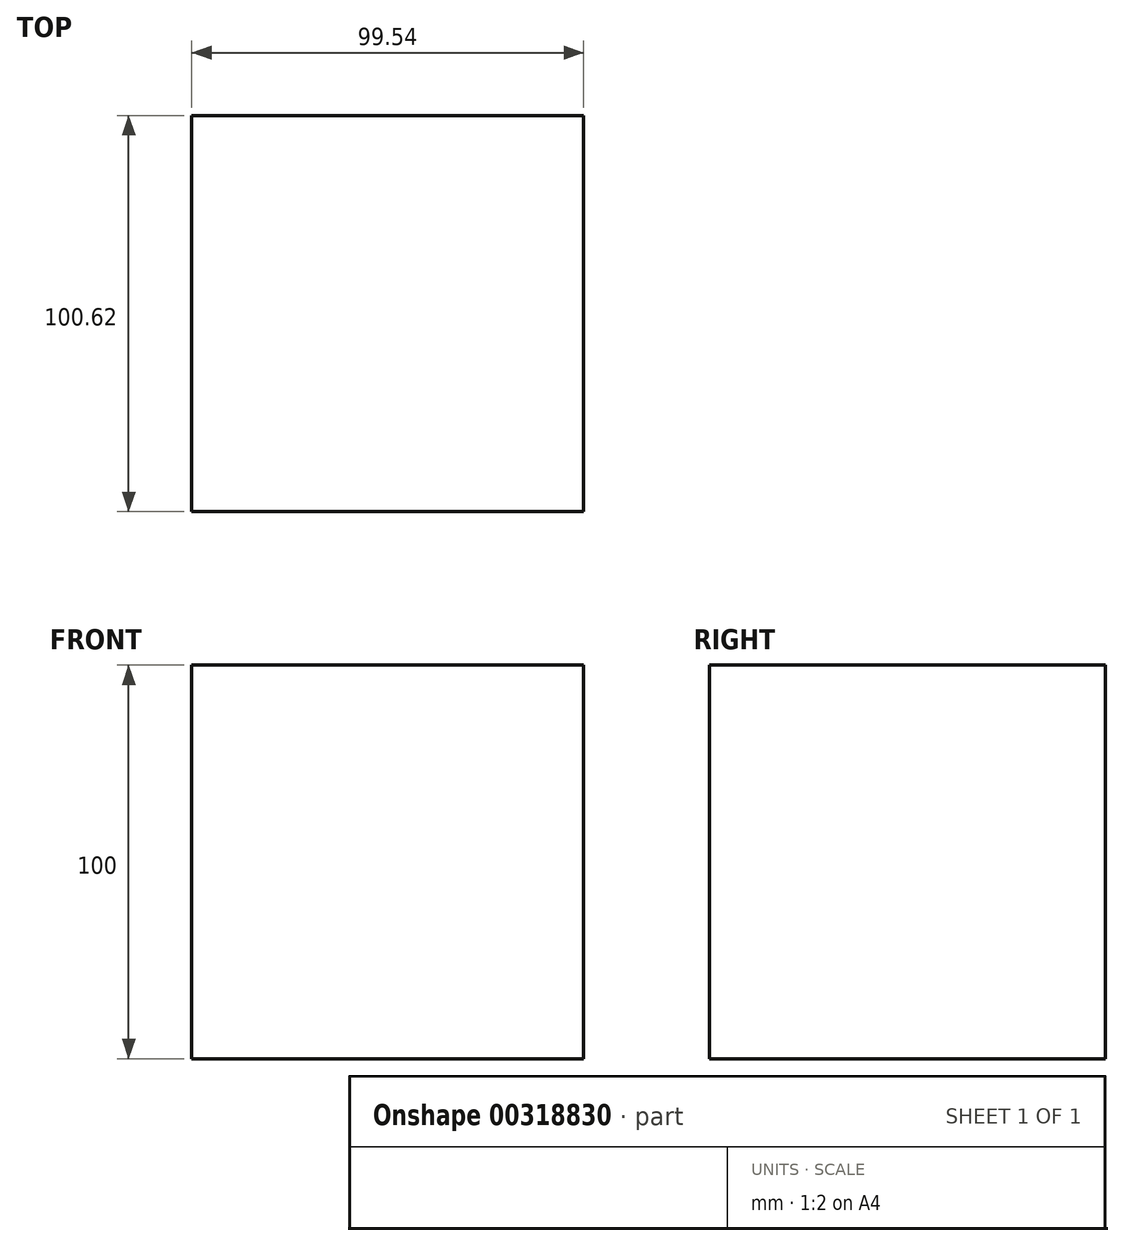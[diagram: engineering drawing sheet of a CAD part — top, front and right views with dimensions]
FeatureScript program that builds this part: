
annotation { "Feature Type Name" : "Feature", "Feature Type Description" : "" }
export const myFeature = defineFeature(function(context is Context, id is Id, definition is map)
    precondition{}
    {
        {
            var Q0;
            Q0=qCreatedBy(makeId("Top.planeOp"),FACE);
            var sketch = newSketch(context, id + "F0", { "sketchPlane" : qUnion([Q0])});
            skLineSegment(sketch, "E0.bottom", {"start": v(49.77, 50.3) * mm, "end": v(-49.77, 50.3) * mm});
            skLineSegment(sketch, "E0.top", {"start": v(49.77, -50.3) * mm, "end": v(-49.77, -50.3) * mm});
            skLineSegment(sketch, "E0.left", {"start": v(49.77, 50.3) * mm, "end": v(49.77, -50.3) * mm});
            skLineSegment(sketch, "E0.right", {"start": v(-49.77, 50.3) * mm, "end": v(-49.77, -50.3) * mm});
            skPoint(sketch, "E0.middle", {"position": v(0, 0) * mm});
            skSolve(sketch);
        }
        {
            var Q0;
            Q0=makeQuery(id+"F0.imprint","IMPRINT",FACE,{"disambiguationData":[TD([[makeQuery(id+"F0.imprint","IMPRINT",EDGE,{"derivedFrom":sQuery(id+"F0.wireOp",EDGE,"E0.bottom")}),1.0]])]});
            extrude(context, id + "F1", {"entities" : qUnion([Q0]), "depth" : 100 * mm});
        }
    });
